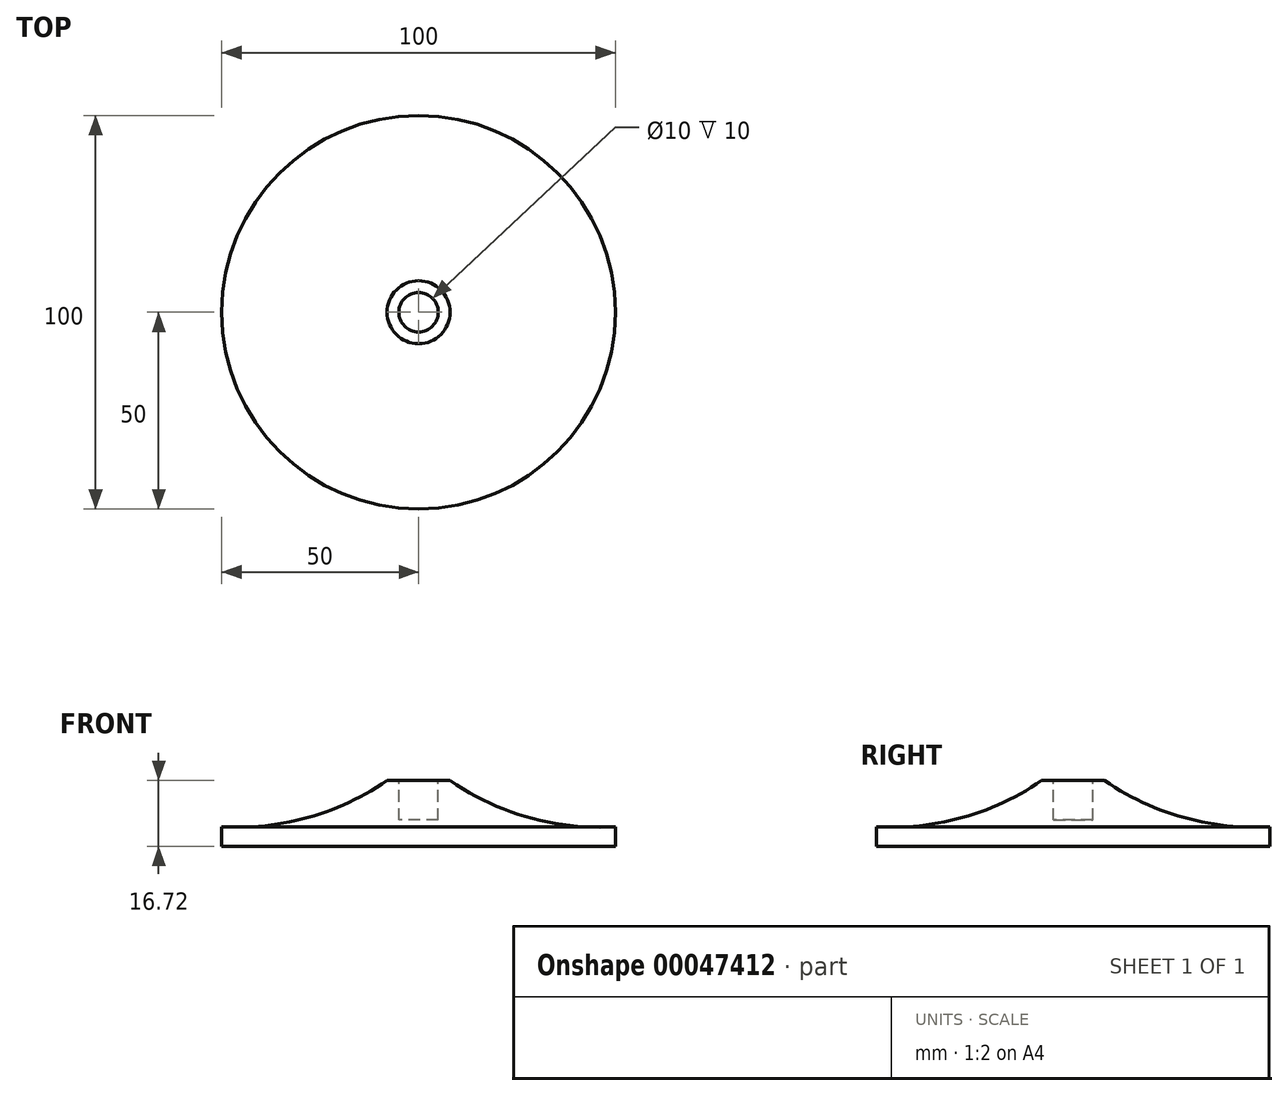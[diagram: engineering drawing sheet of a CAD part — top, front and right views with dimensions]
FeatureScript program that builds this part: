
annotation { "Feature Type Name" : "Feature", "Feature Type Description" : "" }
export const myFeature = defineFeature(function(context is Context, id is Id, definition is map)
    precondition{}
    {
        {
            var Q0;
            Q0=qCreatedBy(makeId("Front.planeOp"),FACE);
            var sketch = newSketch(context, id + "F0", { "sketchPlane" : qUnion([Q0])});
            skLineSegment(sketch, "E0", {"start": v(0, 0) * mm, "end": v(-50, 0) * mm});
            skLineSegment(sketch, "E1", {"start": v(-50, 0) * mm, "end": v(-50, 5) * mm});
            skArc(sketch, "E2", {"start": v(-50, 5) * mm, "mid": v(-28.02, 7.36) * mm, "end": v(-8, 16.72) * mm});
            skLineSegment(sketch, "E3", {"start": v(-8, 16.72) * mm, "end": v(-5, 16.72) * mm});
            skLineSegment(sketch, "E4", {"start": v(-5, 16.72) * mm, "end": v(-5, 6.72) * mm});
            skLineSegment(sketch, "E5", {"start": v(-5, 6.72) * mm, "end": v(0, 6.72) * mm});
            skLineSegment(sketch, "E6", {"start": v(0, 6.72) * mm, "end": v(0, 0) * mm});
            skSolve(sketch);
        }
        {
            var Q0;
            Q0 = qSketchRegion(id + "F0", true);
            var Q1;
            Q1=sQuery(id+"F0.wireOp",EDGE,"E6");
            revolve(context, id + "F1", {"entities" : qUnion([Q0]), "axis" : qUnion([Q1]), "revolveType" : RevolveType.FULL});
        }
    });
